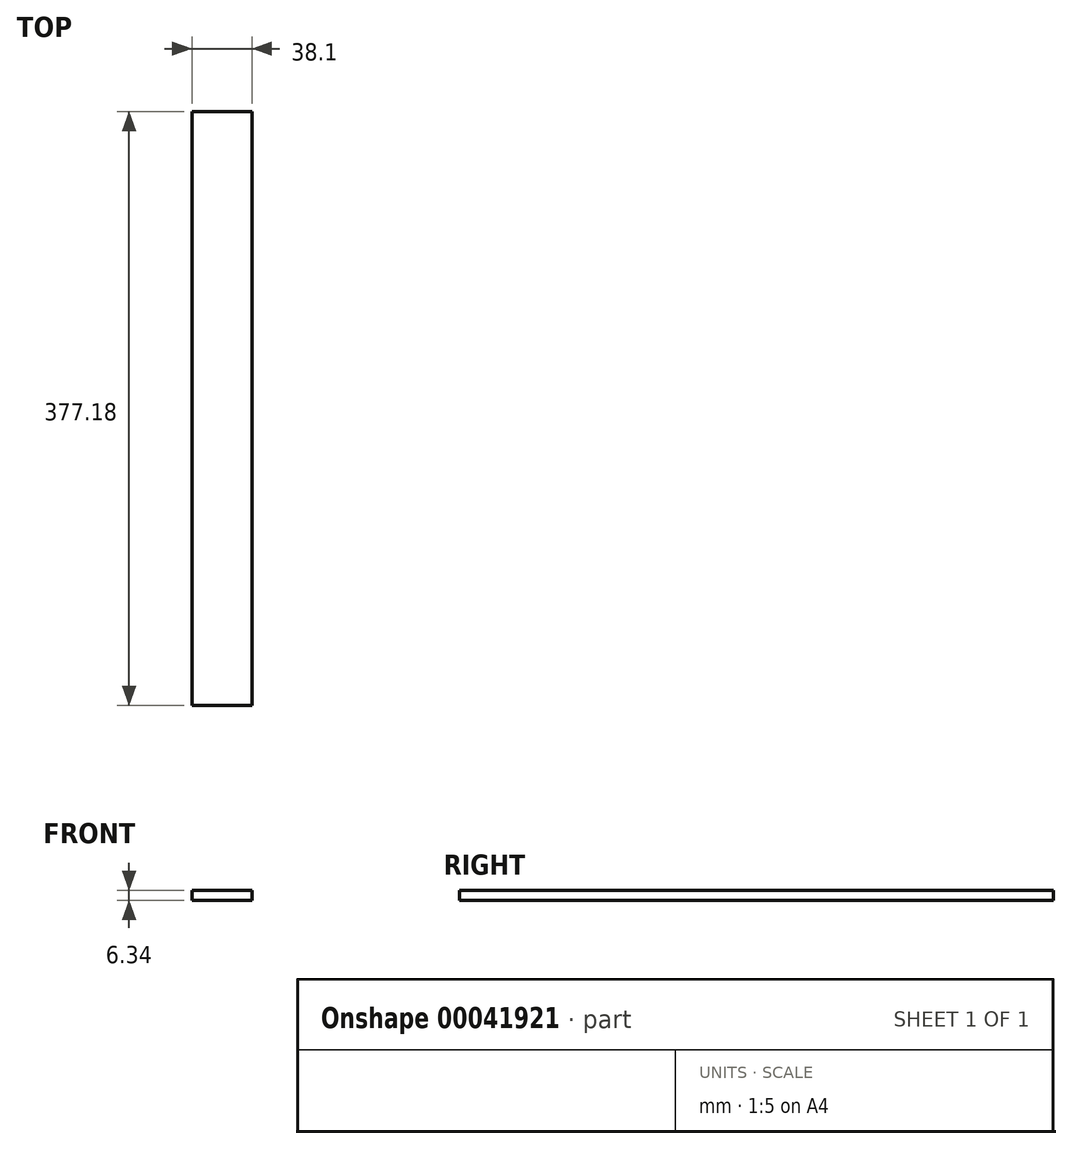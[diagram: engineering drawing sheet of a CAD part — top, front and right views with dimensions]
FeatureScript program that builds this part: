
annotation { "Feature Type Name" : "Feature", "Feature Type Description" : "" }
export const myFeature = defineFeature(function(context is Context, id is Id, definition is map)
    precondition{}
    {
        {
            var Q0;
            Q0=qCreatedBy(makeId("Front.planeOp"),FACE);
            var sketch = newSketch(context, id + "F0", { "sketchPlane" : qUnion([Q0])});
            skLineSegment(sketch, "E0.rect.bottom", {"start": v(19.05, 3.18) * mm, "end": v(-19.05, 3.18) * mm});
            skLineSegment(sketch, "E0.rect.top", {"start": v(19.05, -3.18) * mm, "end": v(-19.05, -3.18) * mm});
            skLineSegment(sketch, "E0.rect.left", {"start": v(19.05, 3.18) * mm, "end": v(19.05, -3.18) * mm});
            skLineSegment(sketch, "E0.rect.right", {"start": v(-19.05, 3.18) * mm, "end": v(-19.05, -3.18) * mm});
            skPoint(sketch, "E0.rect.middle", {"position": v(0, 0) * mm});
            skSolve(sketch);
        }
        {
            var Q0;
            Q0=makeQuery(id+"F0.imprint","IMPRINT",FACE,{"disambiguationData":[TD([[makeQuery(id+"F0.imprint","IMPRINT",EDGE,{"derivedFrom":sQuery(id+"F0.wireOp",EDGE,"E0.rect.bottom")}),1.0]])]});
            extrude(context, id + "F1", {"entities" : qUnion([Q0]), "endBound" : BoundingType.SYMMETRIC, "depth" : 377.2 * mm});
        }
    });
